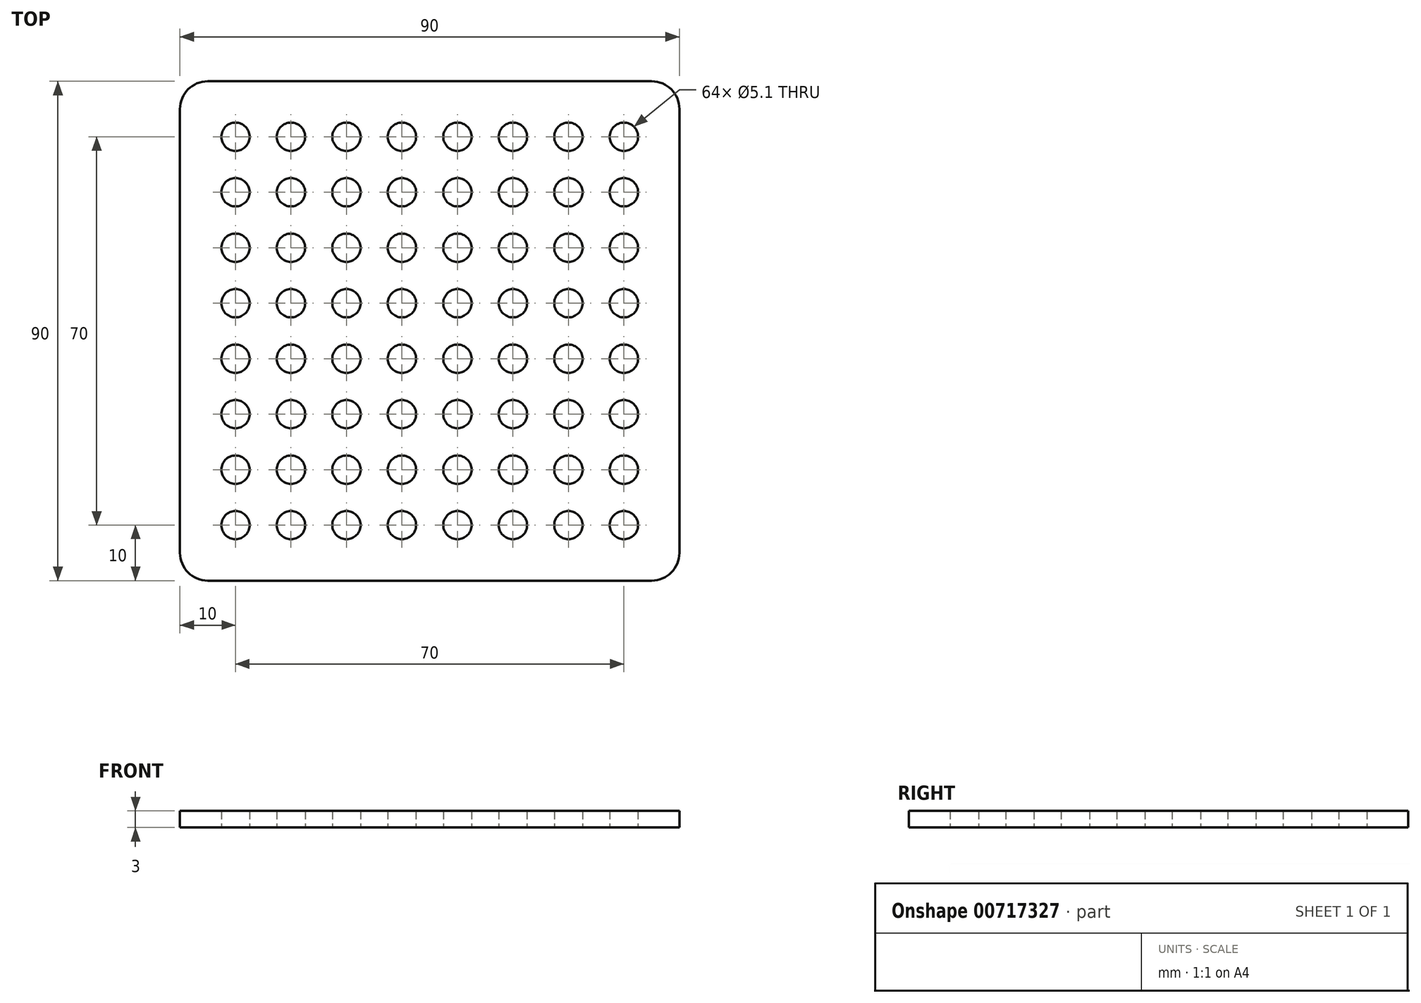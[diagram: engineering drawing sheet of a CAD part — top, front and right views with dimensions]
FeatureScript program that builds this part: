
annotation { "Feature Type Name" : "Feature", "Feature Type Description" : "" }
export const myFeature = defineFeature(function(context is Context, id is Id, definition is map)
    precondition{}
    {
        {
            var Q0;
            Q0=qCreatedBy(makeId("Top.planeOp"),FACE);
            var sketch = newSketch(context, id + "F0", { "sketchPlane" : qUnion([Q0])});
            skLineSegment(sketch, "E0.bottom", {"start": v(-35, 50) * mm, "end": v(45, 50) * mm});
            skLineSegment(sketch, "E0.top", {"start": v(-35, -40) * mm, "end": v(45, -40) * mm});
            skLineSegment(sketch, "E0.left", {"start": v(-40, 45) * mm, "end": v(-40, -35) * mm});
            skLineSegment(sketch, "E0.right", {"start": v(50, 45) * mm, "end": v(50, -35) * mm});
            skCircle(sketch, "E1", {"center": v(-30, 40) * mm, "radius": 2.55 * mm});
            skCircle(sketch, "E2", {"center": v(-20, 40) * mm, "radius": 2.55 * mm});
            skCircle(sketch, "E3", {"center": v(-10, 40) * mm, "radius": 2.55 * mm});
            skCircle(sketch, "E4", {"center": v(0, 40) * mm, "radius": 2.55 * mm});
            skCircle(sketch, "E5", {"center": v(10, 40) * mm, "radius": 2.55 * mm});
            skCircle(sketch, "E6", {"center": v(20, 40) * mm, "radius": 2.55 * mm});
            skCircle(sketch, "E7", {"center": v(30, 40) * mm, "radius": 2.55 * mm});
            skCircle(sketch, "E8", {"center": v(40, 40) * mm, "radius": 2.55 * mm});
            skCircle(sketch, "E9", {"center": v(-30, 30) * mm, "radius": 2.55 * mm});
            skCircle(sketch, "E10", {"center": v(-30, 20) * mm, "radius": 2.55 * mm});
            skCircle(sketch, "E11", {"center": v(-30, 10) * mm, "radius": 2.55 * mm});
            skCircle(sketch, "E12", {"center": v(-30, 0) * mm, "radius": 2.55 * mm});
            skCircle(sketch, "E13", {"center": v(-30, -10) * mm, "radius": 2.55 * mm});
            skCircle(sketch, "E14", {"center": v(-30, -20) * mm, "radius": 2.55 * mm});
            skCircle(sketch, "E15", {"center": v(-30, -30) * mm, "radius": 2.55 * mm});
            skPoint(sketch, "E16.visualSharp", {"position": v(-40, 50) * mm});
            skArc(sketch, "E16.filletArc", {"start": v(-35, 50) * mm, "mid": v(-38.54, 48.54) * mm, "end": v(-40, 45) * mm});
            skPoint(sketch, "E17.visualSharp", {"position": v(50, 50) * mm});
            skArc(sketch, "E17.filletArc", {"start": v(50, 45) * mm, "mid": v(48.54, 48.54) * mm, "end": v(45, 50) * mm});
            skPoint(sketch, "E18.visualSharp", {"position": v(50, -40) * mm});
            skArc(sketch, "E18.filletArc", {"start": v(45, -40) * mm, "mid": v(48.54, -38.54) * mm, "end": v(50, -35) * mm});
            skPoint(sketch, "E19.visualSharp", {"position": v(-40, -40) * mm});
            skArc(sketch, "E19.filletArc", {"start": v(-40, -35) * mm, "mid": v(-38.54, -38.54) * mm, "end": v(-35, -40) * mm});
            skCircle(sketch, "E20", {"center": v(-20, 30) * mm, "radius": 2.55 * mm});
            skCircle(sketch, "E21", {"center": v(-10, 30) * mm, "radius": 2.55 * mm});
            skCircle(sketch, "E22", {"center": v(0, 30) * mm, "radius": 2.55 * mm});
            skCircle(sketch, "E23", {"center": v(10, 30) * mm, "radius": 2.55 * mm});
            skCircle(sketch, "E24", {"center": v(20, 30) * mm, "radius": 2.55 * mm});
            skCircle(sketch, "E25", {"center": v(30, 30) * mm, "radius": 2.55 * mm});
            skCircle(sketch, "E26", {"center": v(40, 30) * mm, "radius": 2.55 * mm});
            skCircle(sketch, "E27", {"center": v(-20, 20) * mm, "radius": 2.55 * mm});
            skCircle(sketch, "E28", {"center": v(-10, 20) * mm, "radius": 2.55 * mm});
            skCircle(sketch, "E29", {"center": v(0, 20) * mm, "radius": 2.55 * mm});
            skCircle(sketch, "E30", {"center": v(10, 20) * mm, "radius": 2.55 * mm});
            skCircle(sketch, "E31", {"center": v(20, 20) * mm, "radius": 2.55 * mm});
            skCircle(sketch, "E32", {"center": v(30, 20) * mm, "radius": 2.55 * mm});
            skCircle(sketch, "E33", {"center": v(40, 20) * mm, "radius": 2.55 * mm});
            skCircle(sketch, "E34", {"center": v(-20, 10) * mm, "radius": 2.55 * mm});
            skCircle(sketch, "E35", {"center": v(-10, 10) * mm, "radius": 2.55 * mm});
            skCircle(sketch, "E36", {"center": v(0, 10) * mm, "radius": 2.55 * mm});
            skCircle(sketch, "E37", {"center": v(10, 10) * mm, "radius": 2.55 * mm});
            skCircle(sketch, "E38", {"center": v(20, 10) * mm, "radius": 2.55 * mm});
            skCircle(sketch, "E39", {"center": v(30, 10) * mm, "radius": 2.55 * mm});
            skCircle(sketch, "E40", {"center": v(40, 10) * mm, "radius": 2.55 * mm});
            skCircle(sketch, "E41", {"center": v(-20, 0) * mm, "radius": 2.55 * mm});
            skCircle(sketch, "E42", {"center": v(-10, 0) * mm, "radius": 2.55 * mm});
            skCircle(sketch, "E43", {"center": v(0, 0) * mm, "radius": 2.55 * mm});
            skCircle(sketch, "E44", {"center": v(10, 0) * mm, "radius": 2.55 * mm});
            skCircle(sketch, "E45", {"center": v(20, 0) * mm, "radius": 2.55 * mm});
            skCircle(sketch, "E46", {"center": v(30, 0) * mm, "radius": 2.55 * mm});
            skCircle(sketch, "E47", {"center": v(40, 0) * mm, "radius": 2.55 * mm});
            skCircle(sketch, "E48", {"center": v(-20, -10) * mm, "radius": 2.55 * mm});
            skCircle(sketch, "E49", {"center": v(-10, -10) * mm, "radius": 2.55 * mm});
            skCircle(sketch, "E50", {"center": v(0, -10) * mm, "radius": 2.55 * mm});
            skCircle(sketch, "E51", {"center": v(10, -10) * mm, "radius": 2.55 * mm});
            skCircle(sketch, "E52", {"center": v(20, -10) * mm, "radius": 2.55 * mm});
            skCircle(sketch, "E53", {"center": v(30, -10) * mm, "radius": 2.55 * mm});
            skCircle(sketch, "E54", {"center": v(40, -10) * mm, "radius": 2.55 * mm});
            skCircle(sketch, "E55", {"center": v(-20, -20) * mm, "radius": 2.55 * mm});
            skCircle(sketch, "E56", {"center": v(-10, -20) * mm, "radius": 2.55 * mm});
            skCircle(sketch, "E57", {"center": v(0, -20) * mm, "radius": 2.55 * mm});
            skCircle(sketch, "E58", {"center": v(10, -20) * mm, "radius": 2.55 * mm});
            skCircle(sketch, "E59", {"center": v(20, -20) * mm, "radius": 2.55 * mm});
            skCircle(sketch, "E60", {"center": v(30, -20) * mm, "radius": 2.55 * mm});
            skCircle(sketch, "E61", {"center": v(40, -20) * mm, "radius": 2.55 * mm});
            skCircle(sketch, "E62", {"center": v(-20, -30) * mm, "radius": 2.55 * mm});
            skCircle(sketch, "E63", {"center": v(-10, -30) * mm, "radius": 2.55 * mm});
            skCircle(sketch, "E64", {"center": v(0, -30) * mm, "radius": 2.55 * mm});
            skCircle(sketch, "E65", {"center": v(10, -30) * mm, "radius": 2.55 * mm});
            skCircle(sketch, "E66", {"center": v(20, -30) * mm, "radius": 2.55 * mm});
            skCircle(sketch, "E67", {"center": v(30, -30) * mm, "radius": 2.55 * mm});
            skCircle(sketch, "E68", {"center": v(40, -30) * mm, "radius": 2.55 * mm});
            skSolve(sketch);
        }
        {
            var Q0;
            Q0=makeQuery(id+"F0.imprint","IMPRINT",FACE,{"disambiguationData":[TD([[makeQuery(id+"F0.imprint","IMPRINT",EDGE,{"derivedFrom":sQuery(id+"F0.wireOp",EDGE,"E0.bottom")}),-1.0]])]});
            extrude(context, id + "F1", {"entities" : qUnion([Q0]), "depth" : 3 * mm, "offsetDistance" : 25 * mm});
        }
    });
